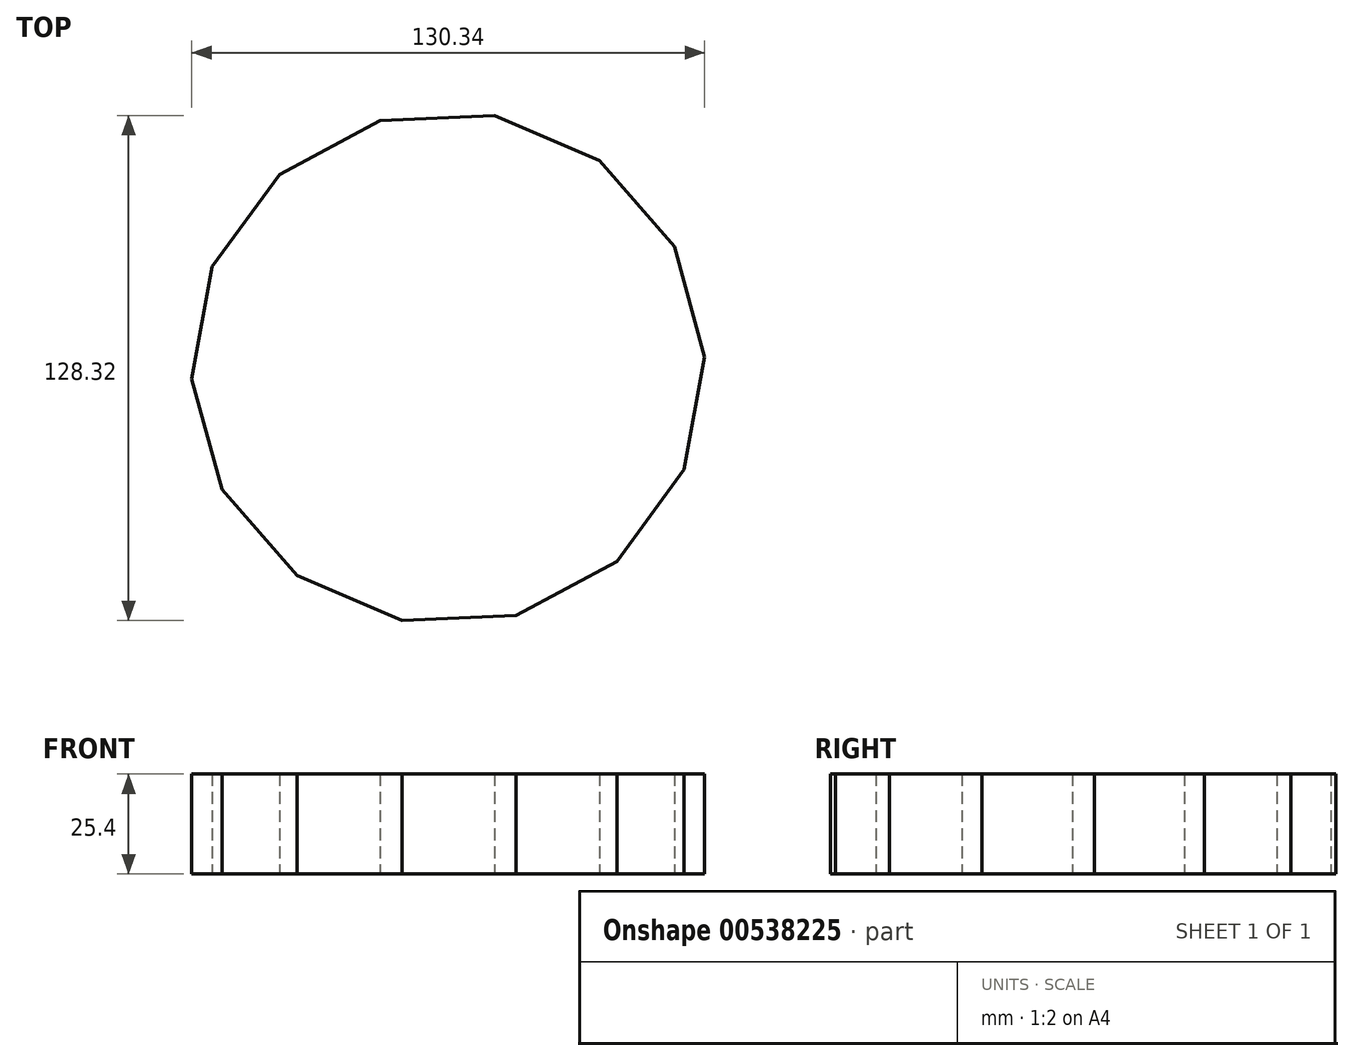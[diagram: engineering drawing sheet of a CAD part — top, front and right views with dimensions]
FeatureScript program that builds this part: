
annotation { "Feature Type Name" : "Feature", "Feature Type Description" : "" }
export const myFeature = defineFeature(function(context is Context, id is Id, definition is map)
    precondition{}
    {
        {
            var Q0;
            Q0=qCreatedBy(makeId("Top.planeOp"),FACE);
            var sketch = newSketch(context, id + "F0", { "sketchPlane" : qUnion([Q0])});
            skCircle(sketch, "E0.cCircle", {"center": v(-216.54, 18) * mm, "radius": 65.23 * mm, "construction": true});
            skLineSegment(sketch, "E0.0", {"start": v(-204.78, 82.17) * mm, "end": v(-178.1, 70.71) * mm});
            skLineSegment(sketch, "E0.1", {"start": v(-178.1, 70.71) * mm, "end": v(-159.04, 48.81) * mm});
            skLineSegment(sketch, "E0.2", {"start": v(-159.04, 48.81) * mm, "end": v(-151.37, 20.82) * mm});
            skLineSegment(sketch, "E0.3", {"start": v(-151.37, 20.82) * mm, "end": v(-156.6, -7.74) * mm});
            skLineSegment(sketch, "E0.4", {"start": v(-156.6, -7.74) * mm, "end": v(-173.72, -31.2) * mm});
            skLineSegment(sketch, "E0.5", {"start": v(-173.72, -31.2) * mm, "end": v(-199.3, -44.9) * mm});
            skLineSegment(sketch, "E0.6", {"start": v(-199.3, -44.9) * mm, "end": v(-228.3, -46.15) * mm});
            skLineSegment(sketch, "E0.7", {"start": v(-228.3, -46.15) * mm, "end": v(-254.98, -34.7) * mm});
            skLineSegment(sketch, "E0.8", {"start": v(-254.98, -34.7) * mm, "end": v(-274.04, -12.8) * mm});
            skLineSegment(sketch, "E0.9", {"start": v(-274.04, -12.8) * mm, "end": v(-281.71, 15.2) * mm});
            skLineSegment(sketch, "E0.10", {"start": v(-281.71, 15.2) * mm, "end": v(-276.48, 43.76) * mm});
            skLineSegment(sketch, "E0.11", {"start": v(-276.48, 43.76) * mm, "end": v(-259.37, 67.21) * mm});
            skLineSegment(sketch, "E0.12", {"start": v(-259.37, 67.21) * mm, "end": v(-233.78, 80.92) * mm});
            skLineSegment(sketch, "E0.13", {"start": v(-233.78, 80.92) * mm, "end": v(-204.78, 82.17) * mm});
            skSolve(sketch);
        }
        {
            var Q0;
            Q0 = qSketchRegion(id + "F0", true);
            extrude(context, id + "F1", {"entities" : qUnion([Q0]), "depth" : 25.4 * mm, "offsetDistance" : 25.4 * mm});
        }
    });
